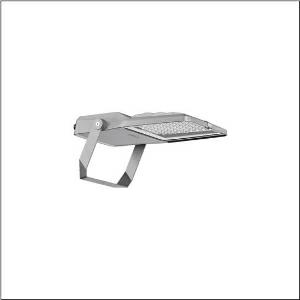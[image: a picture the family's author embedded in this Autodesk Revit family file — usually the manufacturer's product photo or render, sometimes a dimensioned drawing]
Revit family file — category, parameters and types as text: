
# Revit family: floodlight_fl_21_iq_mini___pl64_5xa7772c4e1a_6403
name_source: partatom
category: Lighting Fixtures
units: mm (PartAtom-declared; Revit-internal decimal feet)

## family parameters
Cut with Voids When Loaded = No
Host = Face
Light Source = No
Part Type = Normal
Room Calculation Point = No
Round Connector Dimension = Use Diameter
Shared = No

## types (1)
- --- (1 x LED, 12280 lm, 87.2 W, 4000K)
    Apparent Load = 87 VA
    CIE Flux Codes = 28 80 98 100 100
    Color Rendering = 70
    Color Temperature = 4000K
    Default Elevation = 1800 mm
    Description = Floodlight FL 21 iQ mini, floodlight, primary light control with lens, of PMMA, primary optical cover: protective disc, of toughened safety glass, transparent, light distribution: PL64, light emission: direct distribution, installation type: surface-mounted, lamps: LED, High Power LED, rated values: 12.280lm | 87,2W | 140,8lm/W (begin service life); end service life: 12.280lm | 92,1W; at 50% lumin. flux: 6.140lm | 40,2W | 152,7lm/W, colour temperature: 4000K, colour rendering: CRI > 70, light colour: 740, light setting 1 begin service life: 100% | 12.280lm | 87,2W | 140,8lm/W | 4.000K, light setting 1 end service life: 92,1W, further light settings possible, control: Street-Remote, Auto-Match, Temp-Guard, Night-Set, Smart-Wire, Desk-Remote (wireless, voltage-free reading and setting of iQ features in the workshop via application-optimized NFC function/RFID function), optimised constant luminous flux control (CLO 2.0), pre-setting: linear dimming characteristic, with terminal, 6-pole, mains connection: 220..240V, AC, 50/60Hz, luminaire housing, of diecast aluminium, powder-coated, SITECO metallic grey (DB 702S), corrosivity category C5 mid according to DIN EN ISO 12944suitable for swimming poolschlorine-resistant, sealing non-destructively replaceable, mounting bracket, of steel, galvanised, powder-coated, SITECO metallic grey (DB 702S), protection rating (complete): IP66, insulation class (complete): insulation class II (safety insulation), certification: CE, ENEC, VDE, protection symbol: D, impact resistance: IK08, permissible operating ambient temperature: -40..+40°C, permissible operating ambient temperature for outdoor applications: -40..+50°C, standard: DIN EN 12944, LABS conformity tested according to VDMA 24364:2018-05, packaging unit: 1 piece

Light Distribution: PL64
    Height = 70 mm
    Lamp = 1 x LED
    Lamp Light Flux = 12280 lm
    Lamp Power = 87.2 W
    Lamp count = 1
    Length = 485 mm
    Luminous efficacy = 141 lm/W
    Manufacturer = Siteco
    ModVariant = No
    Model = 5XA7772C4E1A
    Number of Poles = 1
    OnlyDefault = Yes
    Power Factor = 1
    Product Name = Floodlight FL 21 iQ mini | PL64
    Product group = floodlight | pylon annexe
    ProductGroupID = 6201
    Protection Class = Protection class II
    Protection Degree = IP 66
    RLX_Detail_Level = 1
    RLX_Emergency_Light_Flux = 0 lm
    RLX_Emergency_Type = 0
    RLX_Emergency_Type_DB = No
    RlxData = <blob elided: 96525 chars, md5=67ea7463>
    Socket = socket
    Standby Power = 0 W
    System Light Flux = 12280 lm
    System Power = 87 W
    Type Comments = factory setting: luminous flux: 100 % | dim-lin: 254 | 456 mA
    Type Image = l_1006845.jpg
    URL = http://relux.com
    VarID = @adj_165767
    Voltage = 0 V
    Weight = 0.00 kg
    Width = 337 mm

## geometry (parser evidence)
native form markers: Blend x4, Sweep x13
no freeform markers — native parametric forms only
